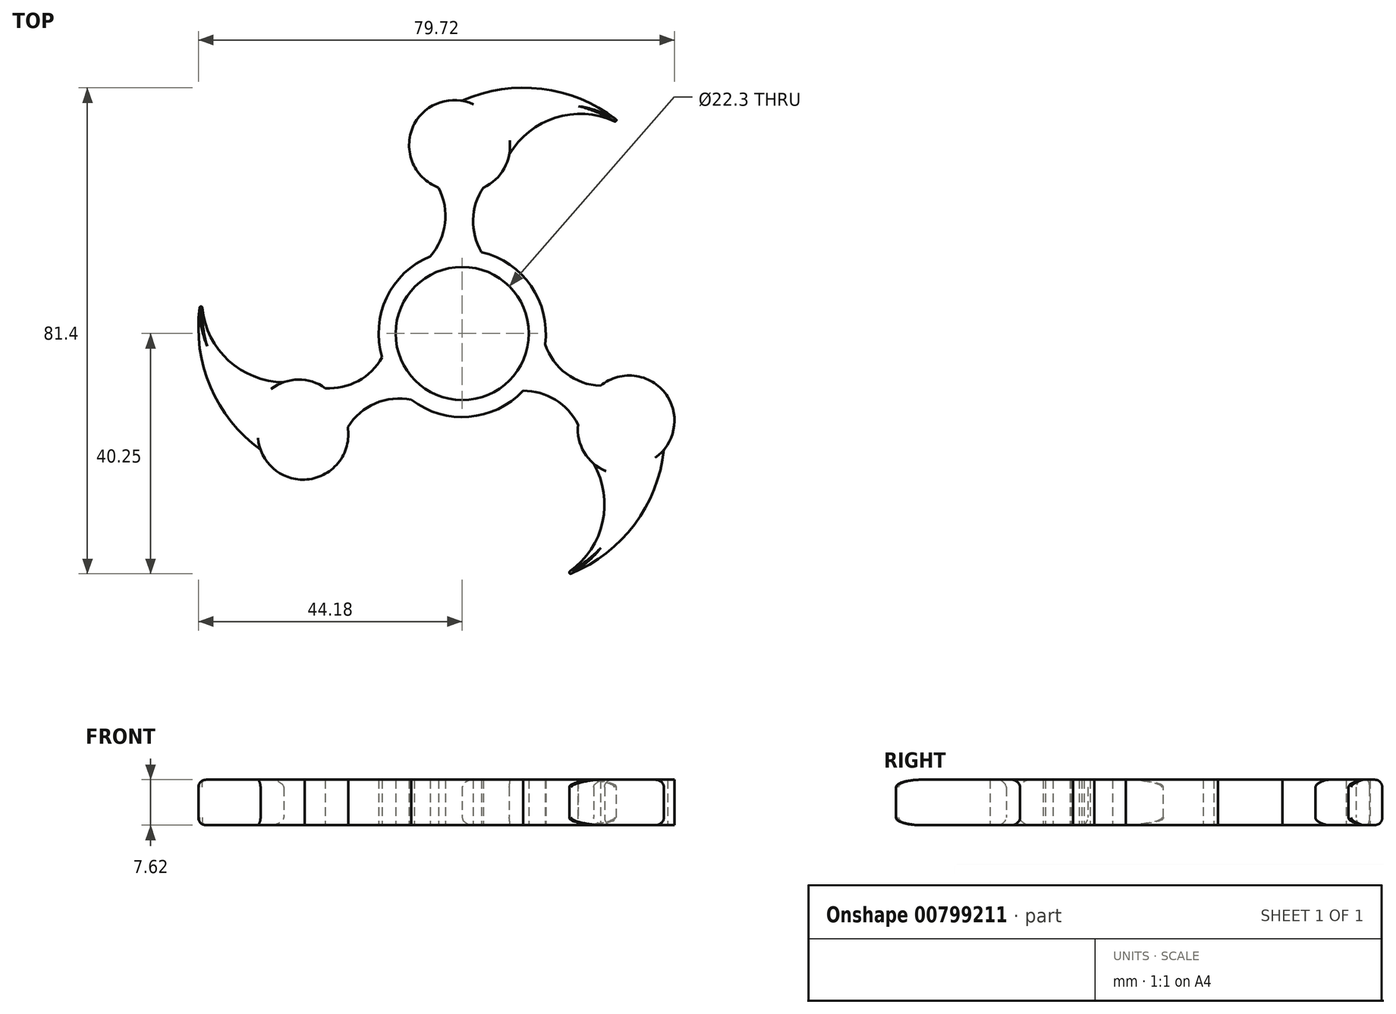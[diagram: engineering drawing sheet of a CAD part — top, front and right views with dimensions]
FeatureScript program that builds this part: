
annotation { "Feature Type Name" : "Feature", "Feature Type Description" : "" }
export const myFeature = defineFeature(function(context is Context, id is Id, definition is map)
    precondition{}
    {
        {
            var Q0;
            Q0=qCreatedBy(makeId("Top.planeOp"),FACE);
            var sketch = newSketch(context, id + "F0", { "sketchPlane" : qUnion([Q0])});
            skCircle(sketch, "E0", {"center": v(0, 0) * mm, "radius": 11.15 * mm});
            skCircle(sketch, "E1", {"center": v(0, 0) * mm, "radius": 14 * mm});
            skArc(sketch, "E2", {"start": v(-5.37, 12.93) * mm, "mid": v(-2.88, 18.46) * mm, "end": v(-3.98, 24.43) * mm});
            skArc(sketch, "E3", {"start": v(3.52, 24.43) * mm, "mid": v(1.82, 19.07) * mm, "end": v(3.23, 13.62) * mm});
            skArc(sketch, "E4", {"start": v(-8.01, 35.1) * mm, "mid": v(-8.4, 28.86) * mm, "end": v(-3.98, 24.43) * mm});
            skArc(sketch, "E5", {"start": v(0, 38.98) * mm, "mid": v(-4.63, 38.34) * mm, "end": v(-8.01, 35.1) * mm});
            skArc(sketch, "E6", {"start": v(3.52, 24.43) * mm, "mid": v(7.8, 33.17) * mm, "end": v(0, 38.98) * mm});
            skArc(sketch, "E7", {"start": v(27.66, 34.27) * mm, "mid": v(14.54, 40.8) * mm, "end": v(0, 38.98) * mm});
            skArc(sketch, "E8", {"start": v(27.66, 34.27) * mm, "mid": v(16.82, 36.47) * mm, "end": v(7.88, 29.95) * mm});
            skArc(sketch, "E9.1.0", {"start": v(-26.4, -24.5) * mm, "mid": v(-20.8, -21.7) * mm, "end": v(-19.16, -15.66) * mm});
            skArc(sketch, "E9.1.1", {"start": v(-8.51, -11.12) * mm, "mid": v(-14.55, -11.72) * mm, "end": v(-19.16, -15.66) * mm});
            skArc(sketch, "E9.1.2", {"start": v(-43.5, 6.82) * mm, "mid": v(-40, -3.67) * mm, "end": v(-29.88, -8.15) * mm});
            skArc(sketch, "E9.1.3", {"start": v(-33.76, -19.5) * mm, "mid": v(-30.88, -23.18) * mm, "end": v(-26.4, -24.5) * mm});
            skArc(sketch, "E9.1.4", {"start": v(-22.92, -9.16) * mm, "mid": v(-32.62, -9.83) * mm, "end": v(-33.76, -19.5) * mm});
            skArc(sketch, "E9.1.5", {"start": v(-22.92, -9.16) * mm, "mid": v(-17.42, -7.96) * mm, "end": v(-13.41, -4.02) * mm});
            skArc(sketch, "E9.1.6", {"start": v(-43.5, 6.82) * mm, "mid": v(-42.6, -7.8) * mm, "end": v(-33.76, -19.5) * mm});
            skArc(sketch, "E9.2.0", {"start": v(34.4, -10.61) * mm, "mid": v(29.2, -7.15) * mm, "end": v(23.15, -8.77) * mm});
            skArc(sketch, "E9.2.1", {"start": v(13.88, -1.81) * mm, "mid": v(17.43, -6.74) * mm, "end": v(23.15, -8.77) * mm});
            skArc(sketch, "E9.2.2", {"start": v(15.85, -41.09) * mm, "mid": v(23.17, -32.8) * mm, "end": v(22, -21.8) * mm});
            skArc(sketch, "E9.2.3", {"start": v(33.76, -19.5) * mm, "mid": v(35.52, -15.16) * mm, "end": v(34.4, -10.61) * mm});
            skArc(sketch, "E9.2.4", {"start": v(19.4, -15.26) * mm, "mid": v(24.82, -23.34) * mm, "end": v(33.76, -19.5) * mm});
            skArc(sketch, "E9.2.5", {"start": v(19.4, -15.26) * mm, "mid": v(15.6, -11.1) * mm, "end": v(10.19, -9.6) * mm});
            skArc(sketch, "E9.2.6", {"start": v(15.85, -41.09) * mm, "mid": v(28.06, -32.99) * mm, "end": v(33.76, -19.5) * mm});
            skSolve(sketch);
        }
        {
            var Q0;
            Q0=makeQuery(id+"F0.imprint","IMPRINT",FACE,{"disambiguationData":[TD([[makeQuery(id+"F0.imprint","IMPRINT",EDGE,{"derivedFrom":sQuery(id+"F0.wireOp",EDGE,"E9.1.0")}),1.0]])]});
            var Q1;
            {var subQ0=sQuery(id+"F0.wireOp",EDGE,"E9.1.2");Q1=makeQuery(id+"F0.imprint","IMPRINT",FACE,{"disambiguationData":[TD([[makeQuery(id+"F0.imprint","IMPRINT",EDGE,{"derivedFrom":subQ0}),-1.0]])]});}
            var Q2;
            Q2=makeQuery(id+"F0.imprint","IMPRINT",FACE,{"disambiguationData":[TD([[makeQuery(id+"F0.imprint","IMPRINT",EDGE,{"derivedFrom":sQuery(id+"F0.wireOp",EDGE,"E0")}),-1.0]])]});
            var Q3;
            Q3=makeQuery(id+"F0.imprint","IMPRINT",FACE,{"disambiguationData":[TD([[makeQuery(id+"F0.imprint","IMPRINT",EDGE,{"derivedFrom":sQuery(id+"F0.wireOp",EDGE,"E9.2.0")}),1.0]])]});
            var Q4;
            {var subQ0=sQuery(id+"F0.wireOp",EDGE,"E9.2.2");Q4=makeQuery(id+"F0.imprint","IMPRINT",FACE,{"disambiguationData":[TD([[makeQuery(id+"F0.imprint","IMPRINT",EDGE,{"derivedFrom":subQ0}),-1.0]])]});}
            var Q5;
            {var subQ1=sQuery(id+"F0.wireOp",EDGE,"E2");Q5=makeQuery(id+"F0.imprint","IMPRINT",FACE,{"disambiguationData":[TD([[makeQuery(id+"F0.imprint","IMPRINT",EDGE,{"derivedFrom":subQ1}),-1.0]])]});}
            var Q6;
            {var subQ0=sQuery(id+"F0.wireOp",EDGE,"E7");Q6=makeQuery(id+"F0.imprint","IMPRINT",FACE,{"disambiguationData":[TD([[makeQuery(id+"F0.imprint","IMPRINT",EDGE,{"derivedFrom":subQ0}),1.0]])]});}
            extrude(context, id + "F1", {"entities" : qUnion([Q0, Q1, Q2, Q3, Q4, Q5, Q6]), "depth" : 7.62 * mm, "offsetDistance" : 25.4 * mm});
        }
        {
            var Q0;
            Q0=makeQuery(id+"F1.opExtrude","SWEPT_EDGE",EDGE,{"disambiguationData":[OSD([sQuery(id+"F0.wireOp",EDGE,"E9.1.2"),sQuery(id+"F0.wireOp",EDGE,"E9.1.6")])]});
            var Q1;
            Q1=makeQuery(id+"F1.opExtrude","SWEPT_EDGE",EDGE,{"disambiguationData":[OSD([sQuery(id+"F0.wireOp",EDGE,"E7"),sQuery(id+"F0.wireOp",EDGE,"E8")])]});
            var Q2;
            Q2=makeQuery(id+"F1.opExtrude","SWEPT_EDGE",EDGE,{"disambiguationData":[OSD([sQuery(id+"F0.wireOp",EDGE,"E9.2.2"),sQuery(id+"F0.wireOp",EDGE,"E9.2.6")])]});
            fillet(context, id + "F2", {"entities" : qUnion([Q0, Q1, Q2]), "radius" : 0.23 * mm, "tangentPropagation" : true, "allowEdgeOverflow" : false});
        }
        {
            var Q0;
            Q0=makeQuery(id+"F1.opExtrude","CAP_EDGE",EDGE,{"disambiguationData":[OSD([sQuery(id+"F0.wireOp",EDGE,"E9.1.6")])],"isStart":false});
            var Q1;
            Q1=makeQuery(id+"F1.opExtrude","CAP_EDGE",EDGE,{"disambiguationData":[OSD([sQuery(id+"F0.wireOp",EDGE,"E7")])],"isStart":false});
            var Q2;
            Q2=makeQuery(id+"F1.opExtrude","CAP_EDGE",EDGE,{"disambiguationData":[OSD([sQuery(id+"F0.wireOp",EDGE,"E9.2.6")])],"isStart":false});
            var Q3;
            Q3=makeQuery(id+"F1.opExtrude","CAP_EDGE",EDGE,{"disambiguationData":[OSD([sQuery(id+"F0.wireOp",EDGE,"E9.1.2")])],"isStart":true});
            var Q4;
            Q4=makeQuery(id+"F1.opExtrude","CAP_EDGE",EDGE,{"disambiguationData":[OSD([sQuery(id+"F0.wireOp",EDGE,"E8")])],"isStart":true});
            var Q5;
            Q5=makeQuery(id+"F1.opExtrude","CAP_EDGE",EDGE,{"disambiguationData":[OSD([sQuery(id+"F0.wireOp",EDGE,"E9.2.2")])],"isStart":true});
            fillet(context, id + "F3", {"entities" : qUnion([Q0, Q1, Q2, Q3, Q4, Q5]), "radius" : 1.27 * mm, "tangentPropagation" : true, "allowEdgeOverflow" : false});
        }
    });
